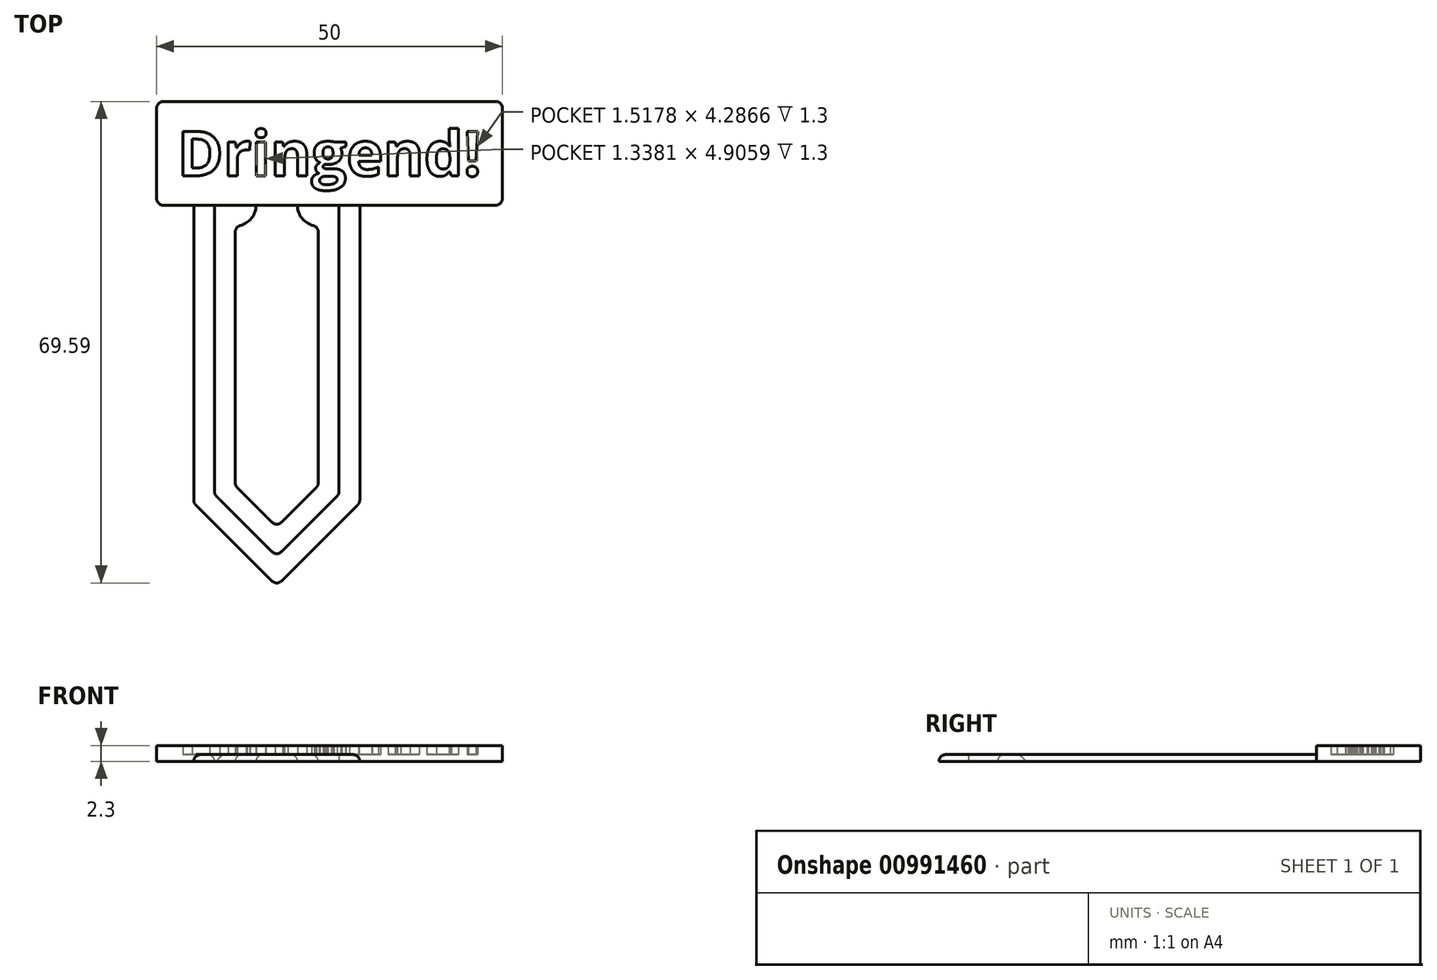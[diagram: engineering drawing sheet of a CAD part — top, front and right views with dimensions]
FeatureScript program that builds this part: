
annotation { "Feature Type Name" : "Feature", "Feature Type Description" : "" }
export const myFeature = defineFeature(function(context is Context, id is Id, definition is map)
    precondition{}
    {
        {
            var Q0;
            Q0=qCreatedBy(makeId("Top.planeOp"),FACE);
            var sketch = newSketch(context, id + "F0", { "sketchPlane" : qUnion([Q0])});
            skLineSegment(sketch, "E0", {"start": v(17.88, 0) * mm, "end": v(17.88, -43) * mm});
            skLineSegment(sketch, "E1", {"start": v(20.88, 0) * mm, "end": v(20.88, -41.76) * mm});
            skLineSegment(sketch, "E2", {"start": v(23.88, -3) * mm, "end": v(23.88, -40.51) * mm});
            skLineSegment(sketch, "E3", {"start": v(29.88, 0) * mm, "end": v(29.88, -27.24) * mm, "construction": true});
            skLineSegment(sketch, "E4", {"start": v(23.88, -40.51) * mm, "end": v(29.88, -46.51) * mm});
            skLineSegment(sketch, "E5", {"start": v(20.88, -41.76) * mm, "end": v(29.88, -50.76) * mm});
            skLineSegment(sketch, "E6", {"start": v(29.88, -55) * mm, "end": v(17.88, -43) * mm});
            skLineSegment(sketch, "E7.MirrorCS", {"start": v(41.88, 0) * mm, "end": v(41.88, -43) * mm});
            skLineSegment(sketch, "E8.MirrorCS", {"start": v(38.88, 0) * mm, "end": v(38.88, -41.76) * mm});
            skLineSegment(sketch, "E9.MirrorCS", {"start": v(35.88, -40.51) * mm, "end": v(29.88, -46.51) * mm});
            skLineSegment(sketch, "E10.MirrorCS", {"start": v(38.88, -41.76) * mm, "end": v(29.88, -50.76) * mm});
            skLineSegment(sketch, "E11.MirrorCS", {"start": v(35.88, -3) * mm, "end": v(35.88, -40.51) * mm});
            skLineSegment(sketch, "E12.MirrorCS", {"start": v(29.88, -55) * mm, "end": v(41.88, -43) * mm});
            skLineSegment(sketch, "E13.bottom", {"start": v(62.5, 0) * mm, "end": v(12.5, 0) * mm});
            skLineSegment(sketch, "E13.top", {"start": v(62.5, 15) * mm, "end": v(12.5, 15) * mm});
            skLineSegment(sketch, "E13.left", {"start": v(62.5, 0) * mm, "end": v(62.5, 15) * mm});
            skLineSegment(sketch, "E13.right", {"start": v(12.5, 0) * mm, "end": v(12.5, 15) * mm});
            skArc(sketch, "E14", {"start": v(26.88, 0) * mm, "mid": v(26, -2.12) * mm, "end": v(23.88, -3) * mm});
            skArc(sketch, "E15", {"start": v(32.88, 0) * mm, "mid": v(33.76, -2.12) * mm, "end": v(35.88, -3) * mm});
            skText(sketch, "E16", { "text": "Dringend!", "fontName": "OpenSans-Bold.ttf"});
            skLineSegment(sketch, "E17", {"start": v(37.5, 15) * mm, "end": v(37.5, 0) * mm, "construction": true});
            skLineSegment(sketch, "E18", {"start": v(12.5, 7.5) * mm, "end": v(62.5, 7.5) * mm, "construction": true});
            const initialGuessF0  = {"E16": [0.0155, 0.00426, 1, 0, 0.00647]};
            skSetInitialGuess(sketch, initialGuessF0);
            skSolve(sketch);
        }
        {
            var Q0;
            {var subQ1=sQuery(id+"F0.wireOp",EDGE,"E0");Q0=makeQuery(id+"F0.imprint","IMPRINT",FACE,{"disambiguationData":[TD([[makeQuery(id+"F0.imprint","IMPRINT",EDGE,{"derivedFrom":subQ1}),1.0]])]});}
            var Q1;
            {var subQ1=sQuery(id+"F0.wireOp",EDGE,"E2");Q1=makeQuery(id+"F0.imprint","IMPRINT",FACE,{"disambiguationData":[TD([[makeQuery(id+"F0.imprint","IMPRINT",EDGE,{"derivedFrom":subQ1}),1.0]])]});}
            var Q2;
            Q2=makeQuery(id+"F0.imprint","IMPRINT",FACE,{"disambiguationData":[TD([[makeQuery(id+"F0.imprint","IMPRINT",EDGE,{"derivedFrom":sQuery(id+"F0.wireOp",EDGE,"E16.sketch_text.stroke-0")}),-1.0]])]});
            var Q3;
            Q3=makeQuery(id+"F0.imprint","IMPRINT",FACE,{"disambiguationData":[TD([[makeQuery(id+"F0.imprint","IMPRINT",EDGE,{"derivedFrom":sQuery(id+"F0.wireOp",EDGE,"E16.sketch_text.stroke-12")}),-1.0]])]});
            var Q4;
            Q4=makeQuery(id+"F0.imprint","IMPRINT",FACE,{"disambiguationData":[TD([[makeQuery(id+"F0.imprint","IMPRINT",EDGE,{"derivedFrom":sQuery(id+"F0.wireOp",EDGE,"E16.sketch_text.stroke-30")}),-1.0]])]});
            var Q5;
            Q5=makeQuery(id+"F0.imprint","IMPRINT",FACE,{"disambiguationData":[TD([[makeQuery(id+"F0.imprint","IMPRINT",EDGE,{"derivedFrom":sQuery(id+"F0.wireOp",EDGE,"E16.sketch_text.stroke-25")}),-1.0]])]});
            var Q6;
            Q6=makeQuery(id+"F0.imprint","IMPRINT",FACE,{"disambiguationData":[TD([[makeQuery(id+"F0.imprint","IMPRINT",EDGE,{"derivedFrom":sQuery(id+"F0.wireOp",EDGE,"E16.sketch_text.stroke-34")}),-1.0]])]});
            var Q7;
            Q7=makeQuery(id+"F0.imprint","IMPRINT",FACE,{"disambiguationData":[TD([[makeQuery(id+"F0.imprint","IMPRINT",EDGE,{"derivedFrom":sQuery(id+"F0.wireOp",EDGE,"E16.sketch_text.stroke-51")}),-1.0]])]});
            var Q8;
            Q8=makeQuery(id+"F0.imprint","IMPRINT",FACE,{"disambiguationData":[TD([[makeQuery(id+"F0.imprint","IMPRINT",EDGE,{"derivedFrom":sQuery(id+"F0.wireOp",EDGE,"E16.sketch_text.stroke-95")}),-1.0]])]});
            var Q9;
            Q9=makeQuery(id+"F0.imprint","IMPRINT",FACE,{"disambiguationData":[TD([[makeQuery(id+"F0.imprint","IMPRINT",EDGE,{"derivedFrom":sQuery(id+"F0.wireOp",EDGE,"E16.sketch_text.stroke-115")}),-1.0]])]});
            var Q10;
            Q10=makeQuery(id+"F0.imprint","IMPRINT",FACE,{"disambiguationData":[TD([[makeQuery(id+"F0.imprint","IMPRINT",EDGE,{"derivedFrom":sQuery(id+"F0.wireOp",EDGE,"E16.sketch_text.stroke-132")}),-1.0]])]});
            var Q11;
            Q11=makeQuery(id+"F0.imprint","IMPRINT",FACE,{"disambiguationData":[TD([[makeQuery(id+"F0.imprint","IMPRINT",EDGE,{"derivedFrom":sQuery(id+"F0.wireOp",EDGE,"E16.sketch_text.stroke-155")}),-1.0]])]});
            var Q12;
            Q12=makeQuery(id+"F0.imprint","IMPRINT",FACE,{"disambiguationData":[TD([[makeQuery(id+"F0.imprint","IMPRINT",EDGE,{"derivedFrom":sQuery(id+"F0.wireOp",EDGE,"E16.sketch_text.stroke-159")}),-1.0]])]});
            extrude(context, id + "F1", {"entities" : qUnion([Q0, Q1, Q2, Q3, Q4, Q5, Q6, Q7, Q8, Q9, Q10, Q11, Q12]), "depth" : 1 * mm, "offsetDistance" : 25 * mm});
        }
        {
            var Q0;
            Q0=makeQuery(id+"F0.imprint","IMPRINT",FACE,{"disambiguationData":[TD([[makeQuery(id+"F0.imprint","IMPRINT",EDGE,{"derivedFrom":sQuery(id+"F0.wireOp",EDGE,"E13.top")}),1.0]])]});
            var Q1;
            Q1=makeQuery(id+"F0.imprint","IMPRINT",FACE,{"disambiguationData":[TD([[makeQuery(id+"F0.imprint","IMPRINT",EDGE,{"derivedFrom":sQuery(id+"F0.wireOp",EDGE,"E16.sketch_text.stroke-7")}),1.0]])]});
            var Q2;
            Q2=makeQuery(id+"F0.imprint","IMPRINT",FACE,{"disambiguationData":[TD([[makeQuery(id+"F0.imprint","IMPRINT",EDGE,{"derivedFrom":sQuery(id+"F0.wireOp",EDGE,"E16.sketch_text.stroke-89")}),1.0]])]});
            var Q3;
            Q3=makeQuery(id+"F0.imprint","IMPRINT",FACE,{"disambiguationData":[TD([[makeQuery(id+"F0.imprint","IMPRINT",EDGE,{"derivedFrom":sQuery(id+"F0.wireOp",EDGE,"E16.sketch_text.stroke-80")}),1.0]])]});
            var Q4;
            Q4=makeQuery(id+"F0.imprint","IMPRINT",FACE,{"disambiguationData":[TD([[makeQuery(id+"F0.imprint","IMPRINT",EDGE,{"derivedFrom":sQuery(id+"F0.wireOp",EDGE,"E16.sketch_text.stroke-95")}),1.0]])]});
            var Q5;
            Q5=makeQuery(id+"F0.imprint","IMPRINT",FACE,{"disambiguationData":[TD([[makeQuery(id+"F0.imprint","IMPRINT",EDGE,{"derivedFrom":sQuery(id+"F0.wireOp",EDGE,"E16.sketch_text.stroke-146")}),1.0]])]});
            extrude(context, id + "F2", {"entities" : qUnion([Q0, Q1, Q2, Q3, Q4, Q5]), "operationType" : NewBodyOperationType.ADD, "depth" : 2.3 * mm, "offsetDistance" : 25 * mm});
        }
        {
            var Q0;
            Q0=makeQuery(id+"F1.opExtrude","SWEPT_EDGE",EDGE,{"disambiguationData":[OSD([sQuery(id+"F0.wireOp",EDGE,"E0"),sQuery(id+"F0.wireOp",EDGE,"E6")])]});
            var Q1;
            Q1=makeQuery(id+"F1.opExtrude","SWEPT_EDGE",EDGE,{"disambiguationData":[OSD([sQuery(id+"F0.wireOp",EDGE,"E6"),sQuery(id+"F0.wireOp",EDGE,"E12.MirrorCS")])]});
            var Q2;
            Q2=makeQuery(id+"F1.opExtrude","SWEPT_EDGE",EDGE,{"disambiguationData":[OSD([sQuery(id+"F0.wireOp",EDGE,"E2"),sQuery(id+"F0.wireOp",EDGE,"E4")])]});
            var Q3;
            Q3=makeQuery(id+"F1.opExtrude","SWEPT_EDGE",EDGE,{"disambiguationData":[OSD([sQuery(id+"F0.wireOp",EDGE,"E4"),sQuery(id+"F0.wireOp",EDGE,"E9.MirrorCS")])]});
            var Q4;
            Q4=makeQuery(id+"F1.opExtrude","SWEPT_EDGE",EDGE,{"disambiguationData":[OSD([sQuery(id+"F0.wireOp",EDGE,"E7.MirrorCS"),sQuery(id+"F0.wireOp",EDGE,"E12.MirrorCS")])]});
            var Q5;
            Q5=makeQuery(id+"F1.opExtrude","SWEPT_EDGE",EDGE,{"disambiguationData":[OSD([sQuery(id+"F0.wireOp",EDGE,"E9.MirrorCS"),sQuery(id+"F0.wireOp",EDGE,"E11.MirrorCS")])]});
            var Q6;
            Q6=makeQuery(id+"F1.opExtrude","SWEPT_EDGE",EDGE,{"disambiguationData":[OSD([sQuery(id+"F0.wireOp",EDGE,"E1"),sQuery(id+"F0.wireOp",EDGE,"E5")])]});
            var Q7;
            Q7=makeQuery(id+"F1.opExtrude","SWEPT_EDGE",EDGE,{"disambiguationData":[OSD([sQuery(id+"F0.wireOp",EDGE,"E5"),sQuery(id+"F0.wireOp",EDGE,"E10.MirrorCS")])]});
            var Q8;
            Q8=makeQuery(id+"F1.opExtrude","SWEPT_EDGE",EDGE,{"disambiguationData":[OSD([sQuery(id+"F0.wireOp",EDGE,"E8.MirrorCS"),sQuery(id+"F0.wireOp",EDGE,"E10.MirrorCS")])]});
            var Q9;
            Q9=makeQuery(id+"F1.opExtrude","CAP_EDGE",EDGE,{"disambiguationData":[OSD([sQuery(id+"F0.wireOp",EDGE,"E7.MirrorCS")])],"isStart":false});
            var Q10;
            Q10=makeQuery(id+"F1.opExtrude","CAP_EDGE",EDGE,{"disambiguationData":[OSD([sQuery(id+"F0.wireOp",EDGE,"E12.MirrorCS")])],"isStart":false});
            var Q11;
            Q11=makeQuery(id+"F1.opExtrude","CAP_EDGE",EDGE,{"disambiguationData":[OSD([sQuery(id+"F0.wireOp",EDGE,"E6")])],"isStart":false});
            var Q12;
            Q12=makeQuery(id+"F1.opExtrude","CAP_EDGE",EDGE,{"disambiguationData":[OSD([sQuery(id+"F0.wireOp",EDGE,"E0")])],"isStart":false});
            var Q13;
            Q13=makeQuery(id+"F1.opExtrude","CAP_EDGE",EDGE,{"disambiguationData":[OSD([sQuery(id+"F0.wireOp",EDGE,"E4")])],"isStart":false});
            var Q14;
            Q14=makeQuery(id+"F1.opExtrude","CAP_EDGE",EDGE,{"disambiguationData":[OSD([sQuery(id+"F0.wireOp",EDGE,"E2")])],"isStart":false});
            var Q15;
            Q15=makeQuery(id+"F1.opExtrude","CAP_EDGE",EDGE,{"disambiguationData":[OSD([sQuery(id+"F0.wireOp",EDGE,"E9.MirrorCS")])],"isStart":false});
            var Q16;
            Q16=makeQuery(id+"F1.opExtrude","CAP_EDGE",EDGE,{"disambiguationData":[OSD([sQuery(id+"F0.wireOp",EDGE,"E11.MirrorCS")])],"isStart":false});
            var Q17;
            Q17=makeQuery(id+"F1.opExtrude","CAP_EDGE",EDGE,{"disambiguationData":[OSD([sQuery(id+"F0.wireOp",EDGE,"E1")])],"isStart":false});
            var Q18;
            Q18=makeQuery(id+"F2.opExtrude","SWEPT_EDGE",EDGE,{"disambiguationData":[OSD([sQuery(id+"F0.wireOp",EDGE,"E13.bottom"),sQuery(id+"F0.wireOp",EDGE,"E13.right")])]});
            var Q19;
            Q19=makeQuery(id+"F2.opExtrude","SWEPT_EDGE",EDGE,{"disambiguationData":[OSD([sQuery(id+"F0.wireOp",EDGE,"E13.top"),sQuery(id+"F0.wireOp",EDGE,"E13.right")])]});
            var Q20;
            Q20=makeQuery(id+"F2.opExtrude","SWEPT_EDGE",EDGE,{"disambiguationData":[OSD([sQuery(id+"F0.wireOp",EDGE,"E13.top"),sQuery(id+"F0.wireOp",EDGE,"E13.left")])]});
            var Q21;
            Q21=makeQuery(id+"F2.opExtrude","SWEPT_EDGE",EDGE,{"disambiguationData":[OSD([sQuery(id+"F0.wireOp",EDGE,"E13.bottom"),sQuery(id+"F0.wireOp",EDGE,"E13.left")])]});
            var Q22;
            Q22=makeQuery(id+"F1.opExtrude","CAP_EDGE",EDGE,{"disambiguationData":[OSD([sQuery(id+"F0.wireOp",EDGE,"E14")])],"isStart":false});
            var Q23;
            Q23=makeQuery(id+"F1.opExtrude","CAP_EDGE",EDGE,{"disambiguationData":[OSD([sQuery(id+"F0.wireOp",EDGE,"E15")])],"isStart":false});
            var Q24;
            Q24=makeQuery(id+"F1.opExtrude","SWEPT_EDGE",EDGE,{"disambiguationData":[OSD([sQuery(id+"F0.wireOp",EDGE,"E2"),sQuery(id+"F0.wireOp",EDGE,"E14")])]});
            var Q25;
            Q25=makeQuery(id+"F1.opExtrude","SWEPT_EDGE",EDGE,{"disambiguationData":[OSD([sQuery(id+"F0.wireOp",EDGE,"E11.MirrorCS"),sQuery(id+"F0.wireOp",EDGE,"E15")])]});
            fillet(context, id + "F3", {"entities" : qUnion([Q0, Q1, Q2, Q3, Q4, Q5, Q6, Q7, Q8, Q9, Q10, Q11, Q12, Q13, Q14, Q15, Q16, Q17, Q18, Q19, Q20, Q21, Q22, Q23, Q24, Q25]), "radius" : 1 * mm, "tangentPropagation" : true, "allowEdgeOverflow" : false});
        }
    });
